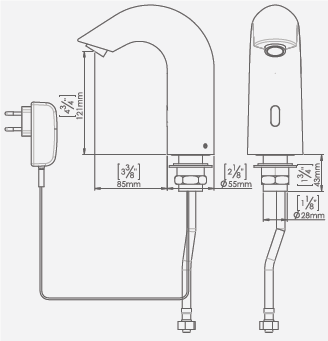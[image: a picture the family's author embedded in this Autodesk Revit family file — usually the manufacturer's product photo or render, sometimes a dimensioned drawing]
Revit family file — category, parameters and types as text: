
# Revit family: Classic E AB1953
name_source: partatom
category: Plumbing Fixtures
revit_build: Autodesk Revit 2015 (Build: 20140322_1515(x64)
units: mm (PartAtom-declared; Revit-internal decimal feet)

## types (1)
- Classic E AB1953
    Assembly Code = D2010.60
    BT_Color = Cromo
    BT_Itemizado_Estandar_CDT = E 04 02 00
    BT_Material = Latón
    BT_SKU = 00 00 00
    BT_Uso = Grifería Lavamanos
    Default Elevation = 1219 mm
    Depth = 140 mm
    Description = Griferia para lavamanos con sensor
    Height = 190 mm
    ID_Objeto = BT_F_F_1796
    ID_Source = BIMTOOL
    Keynote = 22 41 16.16
    Manufacturer = Stern
    Model = Classic E AB1953
    Supplier = Mk
    Type Comments = Grifo electrónico libre de contacto  para instalación a lavabo ó encimera. Activado por sensor de infrarrojos. Versión para agua fría o premezclada . Diseño de una sola pieza en latón cromado. Incluye filtros .Válvula solenoide  situada en el interior del producto,  que lo hace más resistente al vandalismo. Fácil de instalar.    Con el control remoto de Stern pueden cambiarse los siguientes parámetros: rango del sensor, tiempo de seguridad, tiempo de reacción, tiempo de retraso  y encendido-apagado. Opción disponible bajo pedido especial: descarga automática cada 24 horas sin haber hecho uso  del producto. Modelo CLASSIC E AB 1953, marca Stern
    URL = www.mk.cl
    Width = 70 mm

## geometry (parser evidence)
native form markers: Blend x6, Extrusion x2, Sweep x4
no freeform markers — native parametric forms only
